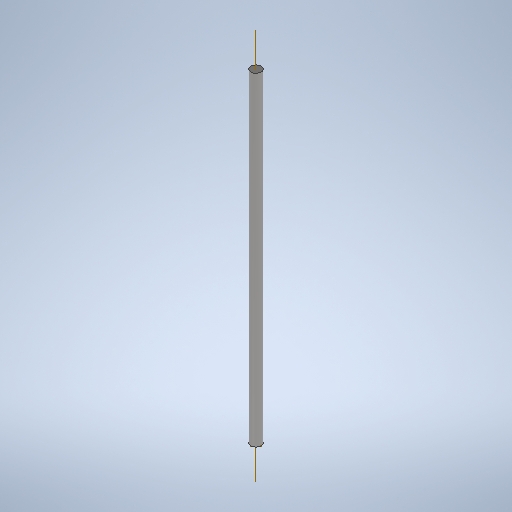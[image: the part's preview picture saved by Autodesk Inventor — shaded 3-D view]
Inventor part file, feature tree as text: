
AUTODESK INVENTOR PART (.ipt)
format: ipt  version: 2025.2 (Build 292293000, 293)  size: 238,592 bytes
history: native  units: mm
features: extrude x1, sketch x1
ambient origin geometry x8: Origin, YZ Plane, XZ Plane, XY Plane, X Axis, Y Axis, Z Axis, Center Point
bodies: Solid1 (feature_tree)
feature tree (2):
  extrude  "Extrusion1"  Depth=250.0mm
  sketch  "Sketch1"  dims[d0=250.0mm d1=0.0mm d6=8.0mm]
